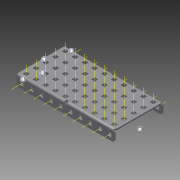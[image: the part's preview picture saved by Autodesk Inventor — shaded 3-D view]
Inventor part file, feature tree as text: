
AUTODESK INVENTOR PART (.ipt)
format: ipt  version: 2015 (Build 190159000, 159)  size: 2,521,600 bytes
history: native  units: in
note: dims shown in document units (in); Inventor stores cm internally (conversion verified against a paired STEP export)
features: other x76, pattern_linear x2, sheet_metal_op x1, extrude x1, imported_body x1, sketch x1
ambient origin geometry x8: Origin, YZ Plane, XZ Plane, XY Plane, X Axis, Y Axis, Z Axis, Center Point
bodies: Body1 (feature_tree)
feature tree (82):
  sheet_metal_op  "Fold1"
  other  "C-Channel"
  extrude  "length cut"  Depth=0.5in
  other  "top axis"
  other  "front axis"
  other  "back axis"
  pattern_linear  "top axes"  Spacing1=0.5in  [1 undecoded]
  pattern_linear  "horiz axes"  Spacing1=0.0in  [1 undecoded]
  other  "right plane"
  imported_body  "Base1"
  sketch  "Sketch1"  dims[d1=0.0in d4=0.5in d5=1.9685in d7=0.5in d10=0.5in d11=0.0in d12=0.0in d13=0.0in d14=-5.0in d15=0.0in d16=0.0in]
  other  "Work Point1"
  other  "Work Axis6"
  other  "Work Axis11"
  other  "Work Axis16"
  other  "Work Axis21"
  other  "Work Point2"
  other  "Work Point3"
  other  "Work Axis36"
  other  "Work Axis37"
  other  "Work Axis38"
  other  "Work Axis39"
  other  "Work Axis40"
  other  "Work Axis41"
  other  "Work Axis60"
  other  "Work Axis61"
  other  "Work Axis62"
  other  "Work Axis63"
  other  "Work Axis64"
  other  "Work Axis65"
  other  "Work Axis84"
  other  "Work Axis85"
  other  "Work Axis86"
  other  "Work Axis87"
  other  "Work Axis88"
  other  "Work Axis89"
  other  "Work Axis108"
  other  "Work Axis109"
  other  "Work Axis110"
  other  "Work Axis111"
  other  "Work Axis112"
  other  "Work Axis113"
  other  "Work Axis132"
  other  "Work Axis133"
  other  "Work Axis134"
  other  "Work Axis135"
  other  "Work Axis136"
  other  "Work Axis137"
  other  "Work Axis156"
  other  "Work Axis157"
  other  "Work Axis158"
  other  "Work Axis159"
  other  "Work Axis160"
  other  "Work Axis161"
  other  "Work Axis180"
  other  "Work Axis181"
  other  "Work Axis182"
  other  "Work Axis183"
  other  "Work Axis184"
  other  "Work Axis185"
  other  "Work Axis204"
  other  "Work Axis205"
  other  "Work Axis206"
  other  "Work Axis232"
  other  "Work Axis233"
  other  "Work Axis234"
  other  "Work Axis260"
  other  "Work Axis261"
  other  "Work Axis262"
  other  "Work Axis288"
  other  "Work Axis289"
  other  "Work Axis290"
  other  "Work Axis316"
  other  "Work Axis317"
  other  "Work Axis318"
  other  "Work Axis344"
  other  "Work Axis345"
  other  "Work Axis346"
  other  "Work Axis372"
  other  "Work Axis373"
  other  "Work Axis374"
  other  "left plane"
note: 2 required parameter values undecoded (feature->parameter linkage not recoverable at this tier; creation-order binding heuristic only, values carry confidence <= 0.55)
